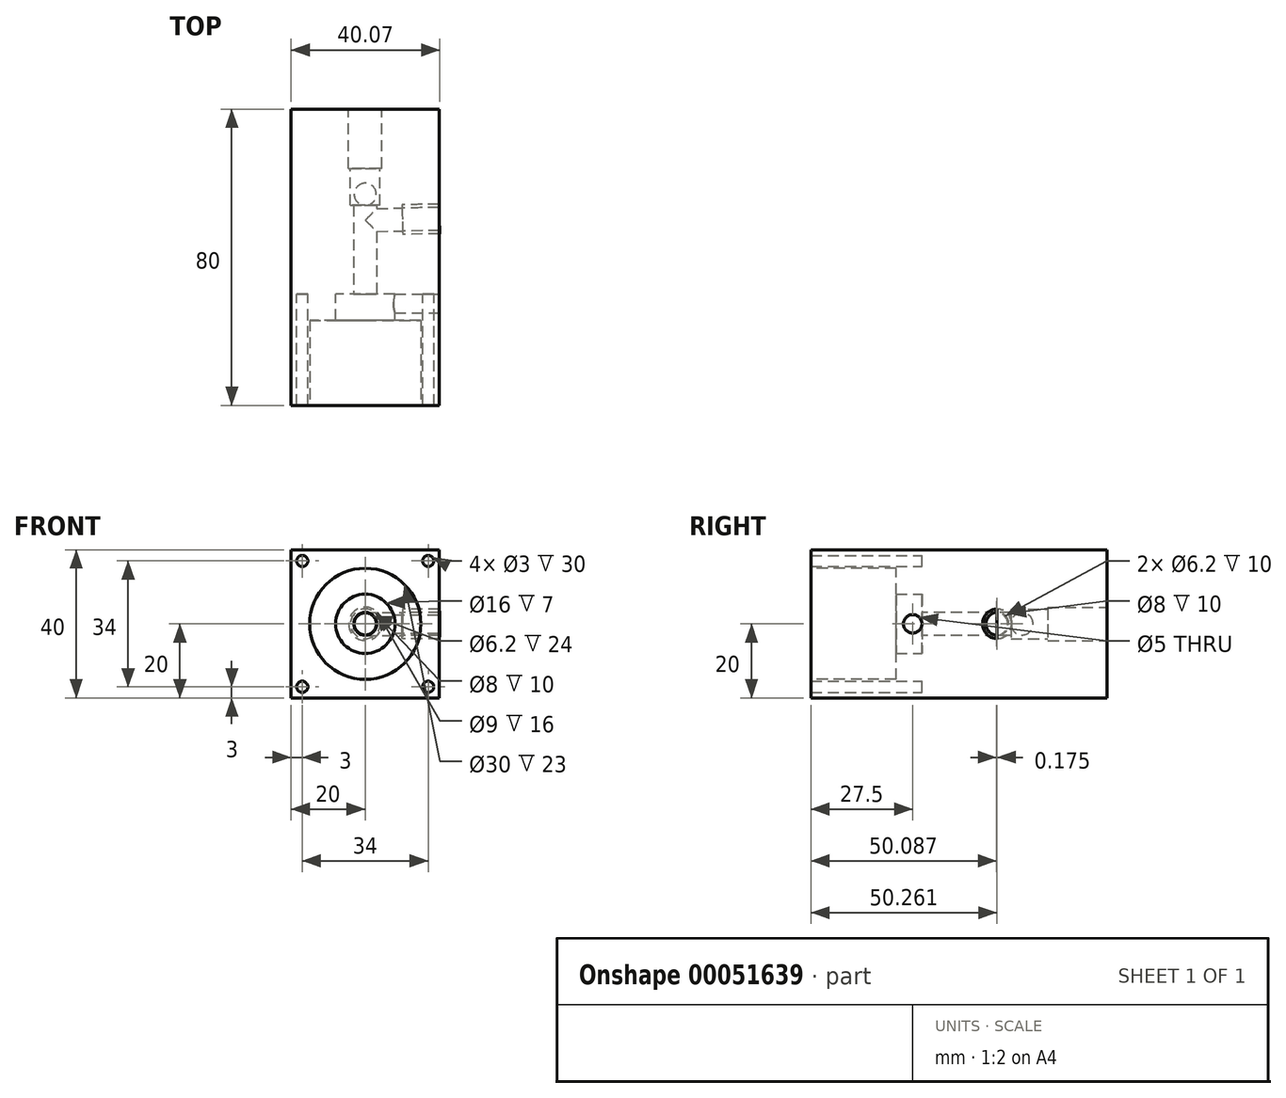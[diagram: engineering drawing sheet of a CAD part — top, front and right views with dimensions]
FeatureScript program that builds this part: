
annotation { "Feature Type Name" : "Feature", "Feature Type Description" : "" }
export const myFeature = defineFeature(function(context is Context, id is Id, definition is map)
    precondition{}
    {
        {
            var Q0;
            Q0=qCreatedBy(makeId("Top.planeOp"),FACE);
            var sketch = newSketch(context, id + "F0", { "sketchPlane" : qUnion([Q0])});
            skLineSegment(sketch, "E0.rect.bottom", {"start": v(20, 50) * mm, "end": v(-20, 50) * mm});
            skLineSegment(sketch, "E0.rect.top", {"start": v(20, -30) * mm, "end": v(-20, -30) * mm});
            skLineSegment(sketch, "E0.rect.left", {"start": v(20, 50) * mm, "end": v(20, -30) * mm});
            skLineSegment(sketch, "E0.rect.right", {"start": v(-20, 50) * mm, "end": v(-20, -30) * mm});
            skPoint(sketch, "E0.rect.middle", {"position": v(0, 0) * mm});
            skSolve(sketch);
        }
        {
            var Q0;
            Q0=qSketchRegion(id+"F0",true);
            extrude(context, id + "F1", {"entities" : qUnion([Q0]), "depth" : 40 * mm, "symmetric" : true});
        }
        {
            var Q0;
            Q0=makeQuery(id+"F1.opExtrude","SWEPT_FACE",FACE,{"disambiguationData":[OSD([sQuery(id+"F0.wireOp",EDGE,"E0.rect.top")])]});
            var sketch = newSketch(context, id + "F2", { "sketchPlane" : qUnion([Q0])});
            skCircle(sketch, "E1", {"center": v(0, 0) * mm, "radius": 3.1 * mm});
            skSolve(sketch);
        }
        {
            var Q0;
            Q0=qSketchRegion(id+"F2",true);
            extrude(context, id + "F3", {"entities" : qUnion([Q0]), "operationType" : NewBodyOperationType.REMOVE, "oppositeDirection" : true, "depth" : 40 * mm});
        }
        {
            var Q0;
            Q0=makeQuery(id+"F1.opExtrude","SWEPT_FACE",FACE,{"disambiguationData":[OSD([sQuery(id+"F0.wireOp",EDGE,"E0.rect.bottom")])]});
            var sketch = newSketch(context, id + "F4", { "sketchPlane" : qUnion([Q0])});
            skCircle(sketch, "E2", {"center": v(0, 0) * mm, "radius": 3.1 * mm});
            skSolve(sketch);
        }
        {
            var Q0;
            Q0=qSketchRegion(id+"F4",true);
            extrude(context, id + "F5", {"entities" : qUnion([Q0]), "operationType" : NewBodyOperationType.REMOVE, "endBound" : BoundingType.THROUGH_ALL, "oppositeDirection" : true, "depth" : 40 * mm});
        }
        {
            var Q0;
            Q0=makeQuery(id+"F1.opExtrude","SWEPT_FACE",FACE,{"disambiguationData":[OSD([sQuery(id+"F0.wireOp",EDGE,"E0.rect.bottom")])]});
            var sketch = newSketch(context, id + "F6", { "sketchPlane" : qUnion([Q0])});
            skCircle(sketch, "E3", {"center": v(0, 0) * mm, "radius": 4 * mm});
            skSolve(sketch);
        }
        {
            var Q0;
            Q0=qSketchRegion(id+"F6",true);
            extrude(context, id + "F7", {"entities" : qUnion([Q0]), "operationType" : NewBodyOperationType.REMOVE, "oppositeDirection" : true, "depth" : 26 * mm});
        }
        {
            var Q0;
            Q0=makeQuery(id+"F1.opExtrude","SWEPT_FACE",FACE,{"disambiguationData":[OSD([sQuery(id+"F0.wireOp",EDGE,"E0.rect.bottom")])]});
            var sketch = newSketch(context, id + "F8", { "sketchPlane" : qUnion([Q0])});
            skCircle(sketch, "E4", {"center": v(0, 0) * mm, "radius": 4.5 * mm});
            skSolve(sketch);
        }
        {
            var Q0;
            Q0=qSketchRegion(id+"F8",true);
            extrude(context, id + "F9", {"entities" : qUnion([Q0]), "operationType" : NewBodyOperationType.REMOVE, "oppositeDirection" : true, "depth" : 16 * mm});
        }
        {
            var Q0;
            Q0=qCreatedBy(makeId("Front.planeOp"),FACE);
            var sketch = newSketch(context, id + "F10", { "sketchPlane" : qUnion([Q0])});
            skCircle(sketch, "E5", {"center": v(-17, 17) * mm, "radius": 1.5 * mm});
            skCircle(sketch, "E6.MirrorC", {"center": v(17, 17) * mm, "radius": 1.5 * mm});
            skCircle(sketch, "E7.MirrorC", {"center": v(-17, -17) * mm, "radius": 1.5 * mm});
            skCircle(sketch, "E8.MirrorC", {"center": v(17, -17) * mm, "radius": 1.5 * mm});
            skCircle(sketch, "E9", {"center": v(0, 0) * mm, "radius": 8 * mm});
            skSolve(sketch);
        }
        {
            var Q0;
            Q0=qSketchRegion(id+"F10",true);
            extrude(context, id + "F11", {"entities" : qUnion([Q0]), "operationType" : NewBodyOperationType.REMOVE, "endBound" : BoundingType.THROUGH_ALL, "depth" : 22 * mm});
        }
        {
            var Q0;
            Q0=qCreatedBy(makeId("Top.planeOp"),FACE);
            var sketch = newSketch(context, id + "F12", { "sketchPlane" : qUnion([Q0])});
            skLineSegment(sketch, "E10", {"start": v(38.24, 20.67) * mm, "end": v(0, 20) * mm, "construction": true});
            skArc(sketch, "E11", {"start": v(9.1, 20.16) * mm, "mid": v(6.05, 23.1) * mm, "end": v(3.1, 20.05) * mm});
            skLineSegment(sketch, "E12", {"start": v(3.1, 20.05) * mm, "end": v(9.1, 20.16) * mm});
            skSolve(sketch);
        }
        {
            var Q0;
            Q0=makeQuery(id+"F12.imprint","IMPRINT",FACE,{"disambiguationData":[TD([[makeQuery(id+"F12.imprint","IMPRINT",EDGE,{"derivedFrom":sQuery(id+"F12.wireOp",EDGE,"E11")}),1.0]])]});
            var Q1;
            Q1=sQuery(id+"F12.wireOp",EDGE,"E10");
            revolve(context, id + "F13", {"entities" : qUnion([Q0]), "axis" : qUnion([Q1]), "revolveType" : RevolveType.FULL});
        }
        {
            var Q0;
            Q0=qCreatedBy(makeId("Top.planeOp"),FACE);
            var sketch = newSketch(context, id + "F14", { "sketchPlane" : qUnion([Q0])});
            skLineSegment(sketch, "E13", {"start": v(0, 29.33) * mm, "end": v(0, -13.58) * mm, "construction": true});
            skArc(sketch, "E14", {"start": v(0, 24) * mm, "mid": v(3, 27) * mm, "end": v(0, 30) * mm});
            skLineSegment(sketch, "E15", {"start": v(0, 30) * mm, "end": v(0, 24) * mm});
            skSolve(sketch);
        }
        {
            var Q0;
            Q0=makeQuery(id+"F14.imprint","IMPRINT",FACE,{"disambiguationData":[TD([[makeQuery(id+"F14.imprint","IMPRINT",EDGE,{"derivedFrom":sQuery(id+"F14.wireOp",EDGE,"E14")}),1.0]])]});
            var Q1;
            Q1=sQuery(id+"F14.wireOp",EDGE,"E13");
            revolve(context, id + "F15", {"entities" : qUnion([Q0]), "axis" : qUnion([Q1]), "revolveType" : RevolveType.FULL});
        }
        {
            var Q0;
            Q0=qCreatedBy(makeId("Top.planeOp"),FACE);
            var sketch = newSketch(context, id + "F16", { "sketchPlane" : qUnion([Q0])});
            skLineSegment(sketch, "E16", {"start": v(0, 20) * mm, "end": v(40, 20.7) * mm, "construction": true});
            skLineSegment(sketch, "E17.bottom", {"start": v(0.05, 16.9) * mm, "end": v(10.05, 17.07) * mm});
            skLineSegment(sketch, "E17.top", {"start": v(0, 20) * mm, "end": v(20, 20.35) * mm});
            skLineSegment(sketch, "E17.left", {"start": v(0.05, 16.9) * mm, "end": v(0, 20) * mm});
            skLineSegment(sketch, "E17.right", {"start": v(20.05, 17.25) * mm, "end": v(20, 20.35) * mm});
            skLineSegment(sketch, "E18", {"start": v(10.05, 17.07) * mm, "end": v(10.07, 16.18) * mm});
            skLineSegment(sketch, "E19", {"start": v(10.07, 16.18) * mm, "end": v(20.07, 16.35) * mm});
            skLineSegment(sketch, "E20", {"start": v(20.07, 16.35) * mm, "end": v(20.05, 17.25) * mm});
            skSolve(sketch);
        }
        {
            var Q0;
            Q0=makeQuery(id+"F16.imprint","IMPRINT",FACE,{"disambiguationData":[TD([[makeQuery(id+"F16.imprint","IMPRINT",EDGE,{"derivedFrom":sQuery(id+"F16.wireOp",EDGE,"E17.bottom")}),1.0]])]});
            var Q1;
            Q1=sQuery(id+"F16.wireOp",EDGE,"E16");
            revolve(context, id + "F17", {"operationType" : NewBodyOperationType.REMOVE, "entities" : qUnion([Q0]), "axis" : qUnion([Q1]), "revolveType" : RevolveType.FULL, "oppositeDirection" : true});
        }
        {
            var Q0;
            Q0=makeQuery(id+"F17.boolean.opBoolean","COPY",FACE,{"derivedFrom":makeQuery(id+"F17.opRevolve","SWEPT_FACE",FACE,{"disambiguationData":[OSD([sQuery(id+"F16.wireOp",EDGE,"E18")])]})});
            var sketch = newSketch(context, id + "F18", { "sketchPlane" : qUnion([Q0])});
            skCircle(sketch, "E21", {"center": v(20, 0) * mm, "radius": 4 * mm});
            skCircle(sketch, "E22", {"center": v(20, 0) * mm, "radius": 3.1 * mm});
            skSolve(sketch);
        }
        {
            var Q0;
            Q0 = qSketchRegion(id + "F18", true);
            extrude(context, id + "F19", {"entities" : qUnion([Q0]), "depth" : 10 * mm});
        }
        {
            var Q0;
            Q0=makeQuery(id+"F1.opExtrude","SWEPT_FACE",FACE,{"disambiguationData":[OSD([sQuery(id+"F0.wireOp",EDGE,"E0.rect.left")])]});
            var sketch = newSketch(context, id + "F20", { "sketchPlane" : qUnion([Q0])});
            skCircle(sketch, "E23", {"center": v(-2.5, 0) * mm, "radius": 2.5 * mm});
            skSolve(sketch);
        }
        {
            var Q0;
            Q0 = qSketchRegion(id + "F20", true);
            extrude(context, id + "F21", {"entities" : qUnion([Q0]), "operationType" : NewBodyOperationType.REMOVE, "oppositeDirection" : true, "depth" : 15 * mm});
        }
        {
            var Q0;
            Q0=makeQuery(id+"F1.opExtrude","SWEPT_FACE",FACE,{"disambiguationData":[OSD([sQuery(id+"F0.wireOp",EDGE,"E0.rect.top")])]});
            var sketch = newSketch(context, id + "F22", { "sketchPlane" : qUnion([Q0])});
            skCircle(sketch, "E24", {"center": v(0, 0) * mm, "radius": 15 * mm});
            skSolve(sketch);
        }
        {
            var Q0;
            Q0 = qSketchRegion(id + "F22", true);
            extrude(context, id + "F23", {"entities" : qUnion([Q0]), "operationType" : NewBodyOperationType.REMOVE, "oppositeDirection" : true, "depth" : 23 * mm});
        }
    });
